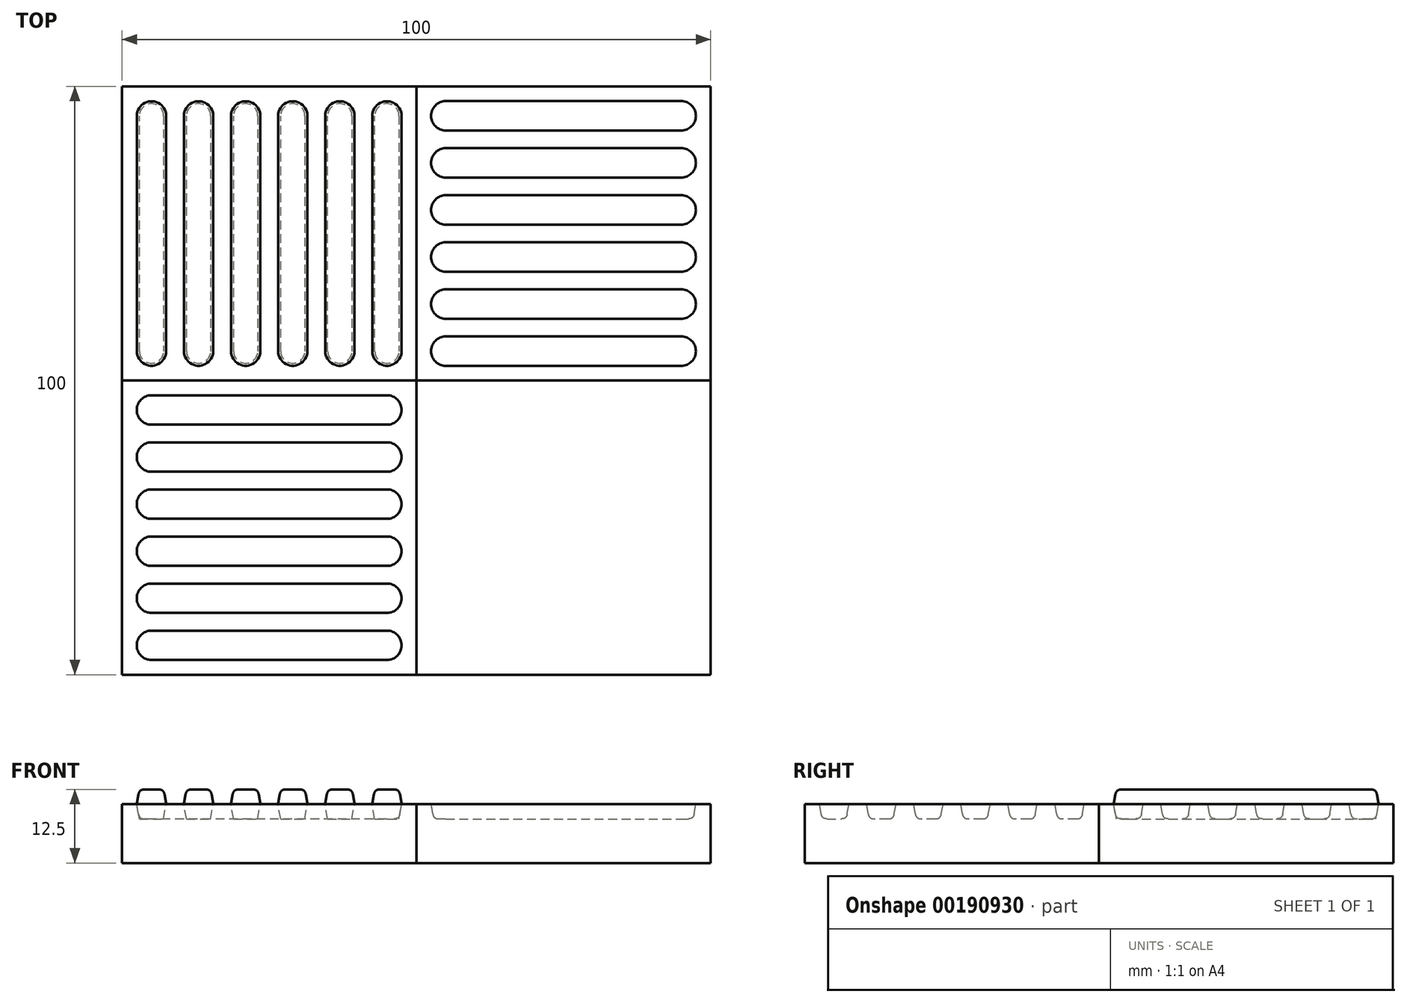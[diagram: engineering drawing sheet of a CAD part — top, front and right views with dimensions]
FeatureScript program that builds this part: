
annotation { "Feature Type Name" : "Feature", "Feature Type Description" : "" }
export const myFeature = defineFeature(function(context is Context, id is Id, definition is map)
    precondition{}
    {
        {
            var Q0;
            Q0=qCreatedBy(makeId("Top.planeOp"),FACE);
            var sketch = newSketch(context, id + "F0", { "sketchPlane" : qUnion([Q0])});
            skLineSegment(sketch, "E0.bottom", {"start": v(0, 0) * mm, "end": v(-50, 0) * mm});
            skLineSegment(sketch, "E0.top", {"start": v(0, 50) * mm, "end": v(-50, 50) * mm});
            skLineSegment(sketch, "E0.left", {"start": v(0, 0) * mm, "end": v(0, 50) * mm});
            skLineSegment(sketch, "E0.right", {"start": v(-50, 0) * mm, "end": v(-50, 50) * mm});
            skPoint(sketch, "E0.middle", {"position": v(-25, 25) * mm});
            skSolve(sketch);
        }
        {
            var Q0;
            Q0=makeQuery(id+"F0.imprint","IMPRINT",FACE,{"disambiguationData":[TD([[makeQuery(id+"F0.imprint","IMPRINT",EDGE,{"derivedFrom":sQuery(id+"F0.wireOp",EDGE,"E0.bottom")}),-1.0]])]});
            extrude(context, id + "F1", {"entities" : qUnion([Q0]), "oppositeDirection" : true, "depth" : 10 * mm});
        }
        {
            var Q0;
            Q0=makeQuery(id+"F1.opExtrude","CAP_FACE",FACE,{"disambiguationData":[OSD([sQuery(id+"F0.wireOp",EDGE,"E0.bottom"),sQuery(id+"F0.wireOp",EDGE,"E0.top"),sQuery(id+"F0.wireOp",EDGE,"E0.left"),sQuery(id+"F0.wireOp",EDGE,"E0.right")])],"isStart":true});
            var sketch = newSketch(context, id + "F2", { "sketchPlane" : qUnion([Q0])});
            skLineSegment(sketch, "E1.bottom", {"start": v(-2.5, 47.5) * mm, "end": v(-47.5, 47.5) * mm, "construction": true});
            skLineSegment(sketch, "E1.top", {"start": v(-2.5, 2.5) * mm, "end": v(-47.5, 2.5) * mm, "construction": true});
            skLineSegment(sketch, "E1.left", {"start": v(-2.5, 47.5) * mm, "end": v(-2.5, 2.5) * mm, "construction": true});
            skLineSegment(sketch, "E1.right", {"start": v(-47.5, 47.5) * mm, "end": v(-47.5, 2.5) * mm, "construction": true});
            skPoint(sketch, "E1.middle", {"position": v(-25, 25) * mm});
            skLineSegment(sketch, "E2", {"start": v(-45, 5) * mm, "end": v(-45, 45) * mm});
            skArc(sketch, "E3.0.startCap", {"start": v(-42.5, 5) * mm, "mid": v(-45, 2.5) * mm, "end": v(-47.5, 5) * mm});
            skArc(sketch, "E3.0.endCap", {"start": v(-47.5, 45) * mm, "mid": v(-45, 47.5) * mm, "end": v(-42.5, 45) * mm});
            skLineSegment(sketch, "E3.0.left", {"start": v(-47.5, 5) * mm, "end": v(-47.5, 45) * mm});
            skLineSegment(sketch, "E3.0.right", {"start": v(-42.5, 5) * mm, "end": v(-42.5, 45) * mm});
            skLineSegment(sketch, "E4.1.0.0", {"start": v(-39.5, 5) * mm, "end": v(-39.5, 45) * mm});
            skArc(sketch, "E4.1.0.1", {"start": v(-39.5, 45) * mm, "mid": v(-37, 47.5) * mm, "end": v(-34.5, 45) * mm});
            skLineSegment(sketch, "E4.1.0.2", {"start": v(-34.5, 5) * mm, "end": v(-34.5, 45) * mm});
            skArc(sketch, "E4.1.0.3", {"start": v(-34.5, 5) * mm, "mid": v(-37, 2.5) * mm, "end": v(-39.5, 5) * mm});
            skLineSegment(sketch, "E4.2.0.0", {"start": v(-31.5, 5) * mm, "end": v(-31.5, 45) * mm});
            skArc(sketch, "E4.2.0.1", {"start": v(-31.5, 45) * mm, "mid": v(-29, 47.5) * mm, "end": v(-26.5, 45) * mm});
            skLineSegment(sketch, "E4.2.0.2", {"start": v(-26.5, 5) * mm, "end": v(-26.5, 45) * mm});
            skArc(sketch, "E4.2.0.3", {"start": v(-26.5, 5) * mm, "mid": v(-29, 2.5) * mm, "end": v(-31.5, 5) * mm});
            skLineSegment(sketch, "E4.3.0.0", {"start": v(-23.5, 5) * mm, "end": v(-23.5, 45) * mm});
            skArc(sketch, "E4.3.0.1", {"start": v(-23.5, 45) * mm, "mid": v(-21, 47.5) * mm, "end": v(-18.5, 45) * mm});
            skLineSegment(sketch, "E4.3.0.2", {"start": v(-18.5, 5) * mm, "end": v(-18.5, 45) * mm});
            skArc(sketch, "E4.3.0.3", {"start": v(-18.5, 5) * mm, "mid": v(-21, 2.5) * mm, "end": v(-23.5, 5) * mm});
            skLineSegment(sketch, "E4.4.0.0", {"start": v(-15.5, 5) * mm, "end": v(-15.5, 45) * mm});
            skArc(sketch, "E4.4.0.1", {"start": v(-15.5, 45) * mm, "mid": v(-13, 47.5) * mm, "end": v(-10.5, 45) * mm});
            skLineSegment(sketch, "E4.4.0.2", {"start": v(-10.5, 5) * mm, "end": v(-10.5, 45) * mm});
            skArc(sketch, "E4.4.0.3", {"start": v(-10.5, 5) * mm, "mid": v(-13, 2.5) * mm, "end": v(-15.5, 5) * mm});
            skLineSegment(sketch, "E4.5.0.0", {"start": v(-7.5, 5) * mm, "end": v(-7.5, 45) * mm});
            skArc(sketch, "E4.5.0.1", {"start": v(-7.5, 45) * mm, "mid": v(-5, 47.5) * mm, "end": v(-2.5, 45) * mm});
            skLineSegment(sketch, "E4.5.0.2", {"start": v(-2.5, 5) * mm, "end": v(-2.5, 45) * mm});
            skArc(sketch, "E4.5.0.3", {"start": v(-2.5, 5) * mm, "mid": v(-5, 2.5) * mm, "end": v(-7.5, 5) * mm});
            skLineSegment(sketch, "E4.direction1", {"start": v(-47.5, 5) * mm, "end": v(-39.5, 5) * mm, "construction": true});
            skSolve(sketch);
        }
        {
            var Q0;
            Q0 = qSketchRegion(id + "F2", true);
            extrude(context, id + "F3", {"entities" : qUnion([Q0]), "depth" : 5 * mm, "hasDraft" : true, "draftAngle" : 10 * degree, "draftPullDirection" : true, "symmetric" : true});
        }
        {
            var Q0;
            Q0=makeQuery(id+"F1.opExtrude","SWEPT_BODY",BODY,{"disambiguationData":[OSD([sQuery(id+"F0.wireOp",EDGE,"E0.bottom"),sQuery(id+"F0.wireOp",EDGE,"E0.top"),sQuery(id+"F0.wireOp",EDGE,"E0.left"),sQuery(id+"F0.wireOp",EDGE,"E0.right")])]});
            var Q1;
            Q1=makeQuery(id+"F3.*.split.splitOp","SPLIT",BODY,{"derivedFrom":makeQuery(id+"F3.opExtrude","SWEPT_BODY",BODY,{"disambiguationData":[OSD([sQuery(id+"F2.wireOp",EDGE,"E3.0.startCap"),sQuery(id+"F2.wireOp",EDGE,"E3.0.endCap"),sQuery(id+"F2.wireOp",EDGE,"E3.0.left"),sQuery(id+"F2.wireOp",EDGE,"E3.0.right")])]})});
            var Q2;
            Q2=makeQuery(id+"F3.*.split.splitOp","SPLIT",BODY,{"derivedFrom":makeQuery(id+"F3.opExtrude","SWEPT_BODY",BODY,{"disambiguationData":[OSD([sQuery(id+"F2.wireOp",EDGE,"E4.1.0.0"),sQuery(id+"F2.wireOp",EDGE,"E4.1.0.1"),sQuery(id+"F2.wireOp",EDGE,"E4.1.0.2"),sQuery(id+"F2.wireOp",EDGE,"E4.1.0.3")])]})});
            var Q3;
            Q3=makeQuery(id+"F3.*.split.splitOp","SPLIT",BODY,{"derivedFrom":makeQuery(id+"F3.opExtrude","SWEPT_BODY",BODY,{"disambiguationData":[OSD([sQuery(id+"F2.wireOp",EDGE,"E4.2.0.0"),sQuery(id+"F2.wireOp",EDGE,"E4.2.0.1"),sQuery(id+"F2.wireOp",EDGE,"E4.2.0.2"),sQuery(id+"F2.wireOp",EDGE,"E4.2.0.3")])]})});
            var Q4;
            Q4=makeQuery(id+"F3.*.split.splitOp","SPLIT",BODY,{"derivedFrom":makeQuery(id+"F3.opExtrude","SWEPT_BODY",BODY,{"disambiguationData":[OSD([sQuery(id+"F2.wireOp",EDGE,"E4.3.0.0"),sQuery(id+"F2.wireOp",EDGE,"E4.3.0.1"),sQuery(id+"F2.wireOp",EDGE,"E4.3.0.2"),sQuery(id+"F2.wireOp",EDGE,"E4.3.0.3")])]})});
            var Q5;
            Q5=makeQuery(id+"F3.*.split.splitOp","SPLIT",BODY,{"derivedFrom":makeQuery(id+"F3.opExtrude","SWEPT_BODY",BODY,{"disambiguationData":[OSD([sQuery(id+"F2.wireOp",EDGE,"E4.4.0.0"),sQuery(id+"F2.wireOp",EDGE,"E4.4.0.1"),sQuery(id+"F2.wireOp",EDGE,"E4.4.0.2"),sQuery(id+"F2.wireOp",EDGE,"E4.4.0.3")])]})});
            var Q6;
            Q6=makeQuery(id+"F3.*.split.splitOp","SPLIT",BODY,{"derivedFrom":makeQuery(id+"F3.opExtrude","SWEPT_BODY",BODY,{"disambiguationData":[OSD([sQuery(id+"F2.wireOp",EDGE,"E4.5.0.0"),sQuery(id+"F2.wireOp",EDGE,"E4.5.0.1"),sQuery(id+"F2.wireOp",EDGE,"E4.5.0.2"),sQuery(id+"F2.wireOp",EDGE,"E4.5.0.3")])]})});
            var Q7;
            Q7=qCreatedBy(makeId("Right.planeOp"),FACE);
            mirror(context, id + "F4", {"entities" : qUnion([Q0, Q1, Q2, Q3, Q4, Q5, Q6]), "mirrorPlane" : qUnion([Q7])});
        }
        {
            var Q0;
            Q0=makeQuery(id+"F4.opPattern","COPY",BODY,{"derivedFrom":makeQuery(id+"F3.*.split.splitOp","SPLIT",BODY,{"derivedFrom":makeQuery(id+"F3.opExtrude","SWEPT_BODY",BODY,{"disambiguationData":[OSD([sQuery(id+"F2.wireOp",EDGE,"E4.5.0.0"),sQuery(id+"F2.wireOp",EDGE,"E4.5.0.1"),sQuery(id+"F2.wireOp",EDGE,"E4.5.0.2"),sQuery(id+"F2.wireOp",EDGE,"E4.5.0.3")])]})}),"instanceName":"1"});
            var Q1;
            Q1=makeQuery(id+"F4.opPattern","COPY",BODY,{"derivedFrom":makeQuery(id+"F3.*.split.splitOp","SPLIT",BODY,{"derivedFrom":makeQuery(id+"F3.opExtrude","SWEPT_BODY",BODY,{"disambiguationData":[OSD([sQuery(id+"F2.wireOp",EDGE,"E4.4.0.0"),sQuery(id+"F2.wireOp",EDGE,"E4.4.0.1"),sQuery(id+"F2.wireOp",EDGE,"E4.4.0.2"),sQuery(id+"F2.wireOp",EDGE,"E4.4.0.3")])]})}),"instanceName":"1"});
            var Q2;
            Q2=makeQuery(id+"F4.opPattern","COPY",BODY,{"derivedFrom":makeQuery(id+"F3.*.split.splitOp","SPLIT",BODY,{"derivedFrom":makeQuery(id+"F3.opExtrude","SWEPT_BODY",BODY,{"disambiguationData":[OSD([sQuery(id+"F2.wireOp",EDGE,"E4.3.0.0"),sQuery(id+"F2.wireOp",EDGE,"E4.3.0.1"),sQuery(id+"F2.wireOp",EDGE,"E4.3.0.2"),sQuery(id+"F2.wireOp",EDGE,"E4.3.0.3")])]})}),"instanceName":"1"});
            var Q3;
            Q3=makeQuery(id+"F4.opPattern","COPY",BODY,{"derivedFrom":makeQuery(id+"F3.*.split.splitOp","SPLIT",BODY,{"derivedFrom":makeQuery(id+"F3.opExtrude","SWEPT_BODY",BODY,{"disambiguationData":[OSD([sQuery(id+"F2.wireOp",EDGE,"E4.2.0.0"),sQuery(id+"F2.wireOp",EDGE,"E4.2.0.1"),sQuery(id+"F2.wireOp",EDGE,"E4.2.0.2"),sQuery(id+"F2.wireOp",EDGE,"E4.2.0.3")])]})}),"instanceName":"1"});
            var Q4;
            Q4=makeQuery(id+"F4.opPattern","COPY",BODY,{"derivedFrom":makeQuery(id+"F3.*.split.splitOp","SPLIT",BODY,{"derivedFrom":makeQuery(id+"F3.opExtrude","SWEPT_BODY",BODY,{"disambiguationData":[OSD([sQuery(id+"F2.wireOp",EDGE,"E4.1.0.0"),sQuery(id+"F2.wireOp",EDGE,"E4.1.0.1"),sQuery(id+"F2.wireOp",EDGE,"E4.1.0.2"),sQuery(id+"F2.wireOp",EDGE,"E4.1.0.3")])]})}),"instanceName":"1"});
            var Q5;
            Q5=makeQuery(id+"F4.opPattern","COPY",BODY,{"derivedFrom":makeQuery(id+"F3.*.split.splitOp","SPLIT",BODY,{"derivedFrom":makeQuery(id+"F3.opExtrude","SWEPT_BODY",BODY,{"disambiguationData":[OSD([sQuery(id+"F2.wireOp",EDGE,"E3.0.startCap"),sQuery(id+"F2.wireOp",EDGE,"E3.0.endCap"),sQuery(id+"F2.wireOp",EDGE,"E3.0.left"),sQuery(id+"F2.wireOp",EDGE,"E3.0.right")])]})}),"instanceName":"1"});
            var Q6;
            Q6=makeQuery(id+"F4.opPattern","COPY",BODY,{"derivedFrom":makeQuery(id+"F1.opExtrude","SWEPT_BODY",BODY,{"disambiguationData":[OSD([sQuery(id+"F0.wireOp",EDGE,"E0.bottom"),sQuery(id+"F0.wireOp",EDGE,"E0.top"),sQuery(id+"F0.wireOp",EDGE,"E0.left"),sQuery(id+"F0.wireOp",EDGE,"E0.right")])]}),"instanceName":"1"});
            booleanBodies(context, id + "F5", {"operationType" : BooleanOperationType.SUBTRACTION, "tools" : qUnion([Q0, Q1, Q2, Q3, Q4, Q5]), "targets" : qUnion([Q6])});
        }
        {
            var Q0;
            Q0=makeQuery(id+"F3.opExtrude","CAP_FACE",FACE,{"disambiguationData":[OSD([sQuery(id+"F2.wireOp",EDGE,"E3.0.startCap"),sQuery(id+"F2.wireOp",EDGE,"E3.0.endCap"),sQuery(id+"F2.wireOp",EDGE,"E3.0.left"),sQuery(id+"F2.wireOp",EDGE,"E3.0.right")])],"isStart":false});
            var Q1;
            Q1=makeQuery(id+"F3.opExtrude","CAP_FACE",FACE,{"disambiguationData":[OSD([sQuery(id+"F2.wireOp",EDGE,"E4.1.0.0"),sQuery(id+"F2.wireOp",EDGE,"E4.1.0.1"),sQuery(id+"F2.wireOp",EDGE,"E4.1.0.2"),sQuery(id+"F2.wireOp",EDGE,"E4.1.0.3")])],"isStart":false});
            var Q2;
            Q2=makeQuery(id+"F3.opExtrude","CAP_FACE",FACE,{"disambiguationData":[OSD([sQuery(id+"F2.wireOp",EDGE,"E4.2.0.0"),sQuery(id+"F2.wireOp",EDGE,"E4.2.0.1"),sQuery(id+"F2.wireOp",EDGE,"E4.2.0.2"),sQuery(id+"F2.wireOp",EDGE,"E4.2.0.3")])],"isStart":false});
            var Q3;
            Q3=makeQuery(id+"F3.opExtrude","CAP_FACE",FACE,{"disambiguationData":[OSD([sQuery(id+"F2.wireOp",EDGE,"E4.3.0.0"),sQuery(id+"F2.wireOp",EDGE,"E4.3.0.1"),sQuery(id+"F2.wireOp",EDGE,"E4.3.0.2"),sQuery(id+"F2.wireOp",EDGE,"E4.3.0.3")])],"isStart":false});
            var Q4;
            Q4=makeQuery(id+"F3.opExtrude","CAP_FACE",FACE,{"disambiguationData":[OSD([sQuery(id+"F2.wireOp",EDGE,"E4.4.0.0"),sQuery(id+"F2.wireOp",EDGE,"E4.4.0.1"),sQuery(id+"F2.wireOp",EDGE,"E4.4.0.2"),sQuery(id+"F2.wireOp",EDGE,"E4.4.0.3")])],"isStart":false});
            var Q5;
            Q5=makeQuery(id+"F3.opExtrude","CAP_FACE",FACE,{"disambiguationData":[OSD([sQuery(id+"F2.wireOp",EDGE,"E4.5.0.0"),sQuery(id+"F2.wireOp",EDGE,"E4.5.0.1"),sQuery(id+"F2.wireOp",EDGE,"E4.5.0.2"),sQuery(id+"F2.wireOp",EDGE,"E4.5.0.3")])],"isStart":false});
            var Q6;
            Q6=makeQuery(id+"F5.opBoolean","COPY",FACE,{"derivedFrom":makeQuery(id+"F4.opPattern","COPY",FACE,{"derivedFrom":makeQuery(id+"F3.opExtrude","CAP_FACE",FACE,{"disambiguationData":[OSD([sQuery(id+"F2.wireOp",EDGE,"E4.5.0.0"),sQuery(id+"F2.wireOp",EDGE,"E4.5.0.1"),sQuery(id+"F2.wireOp",EDGE,"E4.5.0.2"),sQuery(id+"F2.wireOp",EDGE,"E4.5.0.3")])],"isStart":true}),"instanceName":"1"})});
            var Q7;
            Q7=makeQuery(id+"F5.opBoolean","COPY",FACE,{"derivedFrom":makeQuery(id+"F4.opPattern","COPY",FACE,{"derivedFrom":makeQuery(id+"F3.opExtrude","CAP_FACE",FACE,{"disambiguationData":[OSD([sQuery(id+"F2.wireOp",EDGE,"E4.4.0.0"),sQuery(id+"F2.wireOp",EDGE,"E4.4.0.1"),sQuery(id+"F2.wireOp",EDGE,"E4.4.0.2"),sQuery(id+"F2.wireOp",EDGE,"E4.4.0.3")])],"isStart":true}),"instanceName":"1"})});
            var Q8;
            Q8=makeQuery(id+"F5.opBoolean","COPY",FACE,{"derivedFrom":makeQuery(id+"F4.opPattern","COPY",FACE,{"derivedFrom":makeQuery(id+"F3.opExtrude","CAP_FACE",FACE,{"disambiguationData":[OSD([sQuery(id+"F2.wireOp",EDGE,"E4.3.0.0"),sQuery(id+"F2.wireOp",EDGE,"E4.3.0.1"),sQuery(id+"F2.wireOp",EDGE,"E4.3.0.2"),sQuery(id+"F2.wireOp",EDGE,"E4.3.0.3")])],"isStart":true}),"instanceName":"1"})});
            var Q9;
            Q9=makeQuery(id+"F5.opBoolean","COPY",FACE,{"derivedFrom":makeQuery(id+"F4.opPattern","COPY",FACE,{"derivedFrom":makeQuery(id+"F3.opExtrude","CAP_FACE",FACE,{"disambiguationData":[OSD([sQuery(id+"F2.wireOp",EDGE,"E4.2.0.0"),sQuery(id+"F2.wireOp",EDGE,"E4.2.0.1"),sQuery(id+"F2.wireOp",EDGE,"E4.2.0.2"),sQuery(id+"F2.wireOp",EDGE,"E4.2.0.3")])],"isStart":true}),"instanceName":"1"})});
            var Q10;
            Q10=makeQuery(id+"F5.opBoolean","COPY",FACE,{"derivedFrom":makeQuery(id+"F4.opPattern","COPY",FACE,{"derivedFrom":makeQuery(id+"F3.opExtrude","CAP_FACE",FACE,{"disambiguationData":[OSD([sQuery(id+"F2.wireOp",EDGE,"E4.1.0.0"),sQuery(id+"F2.wireOp",EDGE,"E4.1.0.1"),sQuery(id+"F2.wireOp",EDGE,"E4.1.0.2"),sQuery(id+"F2.wireOp",EDGE,"E4.1.0.3")])],"isStart":true}),"instanceName":"1"})});
            var Q11;
            Q11=makeQuery(id+"F5.opBoolean","COPY",FACE,{"derivedFrom":makeQuery(id+"F4.opPattern","COPY",FACE,{"derivedFrom":makeQuery(id+"F3.opExtrude","CAP_FACE",FACE,{"disambiguationData":[OSD([sQuery(id+"F2.wireOp",EDGE,"E3.0.startCap"),sQuery(id+"F2.wireOp",EDGE,"E3.0.endCap"),sQuery(id+"F2.wireOp",EDGE,"E3.0.left"),sQuery(id+"F2.wireOp",EDGE,"E3.0.right")])],"isStart":true}),"instanceName":"1"})});
            fillet(context, id + "F6", {"entities" : qUnion([Q0, Q1, Q2, Q3, Q4, Q5, Q6, Q7, Q8, Q9, Q10, Q11]), "radius" : 1 * mm, "tangentPropagation" : true, "rho" : 0.5, "crossSection" : FilletCrossSection.CONIC, "allowEdgeOverflow" : false});
        }
        {
            var Q0;
            {var subQ0=makeQuery(id+"F3.opExtrude","SWEPT_FACE",FACE,{"disambiguationData":[OSD([sQuery(id+"F2.wireOp",EDGE,"E3.0.left")])]});Q0=makeQuery(id+"F3.*.booleanUnion.opBoolean","MERGE",EDGE,{"derivedFrom":[makeQuery(id+"F3.*.split.splitOp","SPLIT_SURFACE_INTERSECT",EDGE,{"derivedFrom":[subQ0]}),makeQuery(id+"F3.*.split.splitOp","SPLIT_SURFACE_INTERSECT",EDGE,{"derivedFrom":[subQ0],"isFromBackBody":true})]});}
            var Q1;
            {var subQ0=makeQuery(id+"F3.opExtrude","SWEPT_FACE",FACE,{"disambiguationData":[OSD([sQuery(id+"F2.wireOp",EDGE,"E4.1.0.0")])]});Q1=makeQuery(id+"F3.*.booleanUnion.opBoolean","MERGE",EDGE,{"derivedFrom":[makeQuery(id+"F3.*.split.splitOp","SPLIT_SURFACE_INTERSECT",EDGE,{"derivedFrom":[subQ0]}),makeQuery(id+"F3.*.split.splitOp","SPLIT_SURFACE_INTERSECT",EDGE,{"derivedFrom":[subQ0],"isFromBackBody":true})]});}
            var Q2;
            {var subQ0=makeQuery(id+"F3.opExtrude","SWEPT_FACE",FACE,{"disambiguationData":[OSD([sQuery(id+"F2.wireOp",EDGE,"E4.2.0.0")])]});Q2=makeQuery(id+"F3.*.booleanUnion.opBoolean","MERGE",EDGE,{"derivedFrom":[makeQuery(id+"F3.*.split.splitOp","SPLIT_SURFACE_INTERSECT",EDGE,{"derivedFrom":[subQ0]}),makeQuery(id+"F3.*.split.splitOp","SPLIT_SURFACE_INTERSECT",EDGE,{"derivedFrom":[subQ0],"isFromBackBody":true})]});}
            var Q3;
            {var subQ0=makeQuery(id+"F3.opExtrude","SWEPT_FACE",FACE,{"disambiguationData":[OSD([sQuery(id+"F2.wireOp",EDGE,"E4.3.0.0")])]});Q3=makeQuery(id+"F3.*.booleanUnion.opBoolean","MERGE",EDGE,{"derivedFrom":[makeQuery(id+"F3.*.split.splitOp","SPLIT_SURFACE_INTERSECT",EDGE,{"derivedFrom":[subQ0]}),makeQuery(id+"F3.*.split.splitOp","SPLIT_SURFACE_INTERSECT",EDGE,{"derivedFrom":[subQ0],"isFromBackBody":true})]});}
            var Q4;
            {var subQ0=makeQuery(id+"F3.opExtrude","SWEPT_FACE",FACE,{"disambiguationData":[OSD([sQuery(id+"F2.wireOp",EDGE,"E4.4.0.0")])]});Q4=makeQuery(id+"F3.*.booleanUnion.opBoolean","MERGE",EDGE,{"derivedFrom":[makeQuery(id+"F3.*.split.splitOp","SPLIT_SURFACE_INTERSECT",EDGE,{"derivedFrom":[subQ0]}),makeQuery(id+"F3.*.split.splitOp","SPLIT_SURFACE_INTERSECT",EDGE,{"derivedFrom":[subQ0],"isFromBackBody":true})]});}
            var Q5;
            {var subQ0=makeQuery(id+"F3.opExtrude","SWEPT_FACE",FACE,{"disambiguationData":[OSD([sQuery(id+"F2.wireOp",EDGE,"E4.5.0.0")])]});Q5=makeQuery(id+"F3.*.booleanUnion.opBoolean","MERGE",EDGE,{"derivedFrom":[makeQuery(id+"F3.*.split.splitOp","SPLIT_SURFACE_INTERSECT",EDGE,{"derivedFrom":[subQ0]}),makeQuery(id+"F3.*.split.splitOp","SPLIT_SURFACE_INTERSECT",EDGE,{"derivedFrom":[subQ0],"isFromBackBody":true})]});}
            var Q6;
            {var subQ0=makeQuery(id+"F3.opExtrude","SWEPT_FACE",FACE,{"disambiguationData":[OSD([sQuery(id+"F2.wireOp",EDGE,"E4.5.0.2")])]});Q6=makeQuery(id+"F5.opBoolean","COPY",EDGE,{"derivedFrom":makeQuery(id+"F4.opPattern","COPY",EDGE,{"derivedFrom":makeQuery(id+"F3.*.booleanUnion.opBoolean","MERGE",EDGE,{"derivedFrom":[makeQuery(id+"F3.*.split.splitOp","SPLIT_SURFACE_INTERSECT",EDGE,{"derivedFrom":[subQ0]}),makeQuery(id+"F3.*.split.splitOp","SPLIT_SURFACE_INTERSECT",EDGE,{"derivedFrom":[subQ0],"isFromBackBody":true})]}),"instanceName":"1"})});}
            var Q7;
            {var subQ0=makeQuery(id+"F3.opExtrude","SWEPT_FACE",FACE,{"disambiguationData":[OSD([sQuery(id+"F2.wireOp",EDGE,"E4.4.0.2")])]});Q7=makeQuery(id+"F5.opBoolean","COPY",EDGE,{"derivedFrom":makeQuery(id+"F4.opPattern","COPY",EDGE,{"derivedFrom":makeQuery(id+"F3.*.booleanUnion.opBoolean","MERGE",EDGE,{"derivedFrom":[makeQuery(id+"F3.*.split.splitOp","SPLIT_SURFACE_INTERSECT",EDGE,{"derivedFrom":[subQ0]}),makeQuery(id+"F3.*.split.splitOp","SPLIT_SURFACE_INTERSECT",EDGE,{"derivedFrom":[subQ0],"isFromBackBody":true})]}),"instanceName":"1"})});}
            var Q8;
            {var subQ0=makeQuery(id+"F3.opExtrude","SWEPT_FACE",FACE,{"disambiguationData":[OSD([sQuery(id+"F2.wireOp",EDGE,"E4.3.0.2")])]});Q8=makeQuery(id+"F5.opBoolean","COPY",EDGE,{"derivedFrom":makeQuery(id+"F4.opPattern","COPY",EDGE,{"derivedFrom":makeQuery(id+"F3.*.booleanUnion.opBoolean","MERGE",EDGE,{"derivedFrom":[makeQuery(id+"F3.*.split.splitOp","SPLIT_SURFACE_INTERSECT",EDGE,{"derivedFrom":[subQ0]}),makeQuery(id+"F3.*.split.splitOp","SPLIT_SURFACE_INTERSECT",EDGE,{"derivedFrom":[subQ0],"isFromBackBody":true})]}),"instanceName":"1"})});}
            var Q9;
            {var subQ0=makeQuery(id+"F3.opExtrude","SWEPT_FACE",FACE,{"disambiguationData":[OSD([sQuery(id+"F2.wireOp",EDGE,"E4.2.0.2")])]});Q9=makeQuery(id+"F5.opBoolean","COPY",EDGE,{"derivedFrom":makeQuery(id+"F4.opPattern","COPY",EDGE,{"derivedFrom":makeQuery(id+"F3.*.booleanUnion.opBoolean","MERGE",EDGE,{"derivedFrom":[makeQuery(id+"F3.*.split.splitOp","SPLIT_SURFACE_INTERSECT",EDGE,{"derivedFrom":[subQ0]}),makeQuery(id+"F3.*.split.splitOp","SPLIT_SURFACE_INTERSECT",EDGE,{"derivedFrom":[subQ0],"isFromBackBody":true})]}),"instanceName":"1"})});}
            var Q10;
            {var subQ0=makeQuery(id+"F3.opExtrude","SWEPT_FACE",FACE,{"disambiguationData":[OSD([sQuery(id+"F2.wireOp",EDGE,"E4.1.0.2")])]});Q10=makeQuery(id+"F5.opBoolean","COPY",EDGE,{"derivedFrom":makeQuery(id+"F4.opPattern","COPY",EDGE,{"derivedFrom":makeQuery(id+"F3.*.booleanUnion.opBoolean","MERGE",EDGE,{"derivedFrom":[makeQuery(id+"F3.*.split.splitOp","SPLIT_SURFACE_INTERSECT",EDGE,{"derivedFrom":[subQ0]}),makeQuery(id+"F3.*.split.splitOp","SPLIT_SURFACE_INTERSECT",EDGE,{"derivedFrom":[subQ0],"isFromBackBody":true})]}),"instanceName":"1"})});}
            var Q11;
            {var subQ0=makeQuery(id+"F3.opExtrude","SWEPT_FACE",FACE,{"disambiguationData":[OSD([sQuery(id+"F2.wireOp",EDGE,"E3.0.right")])]});Q11=makeQuery(id+"F5.opBoolean","COPY",EDGE,{"derivedFrom":makeQuery(id+"F4.opPattern","COPY",EDGE,{"derivedFrom":makeQuery(id+"F3.*.booleanUnion.opBoolean","MERGE",EDGE,{"derivedFrom":[makeQuery(id+"F3.*.split.splitOp","SPLIT_SURFACE_INTERSECT",EDGE,{"derivedFrom":[subQ0]}),makeQuery(id+"F3.*.split.splitOp","SPLIT_SURFACE_INTERSECT",EDGE,{"derivedFrom":[subQ0],"isFromBackBody":true})]}),"instanceName":"1"})});}
            fillet(context, id + "F7", {"entities" : qUnion([Q0, Q1, Q2, Q3, Q4, Q5, Q6, Q7, Q8, Q9, Q10, Q11]), "radius" : 1 * mm, "tangentPropagation" : true, "rho" : 0.5, "crossSection" : FilletCrossSection.CONIC, "allowEdgeOverflow" : false});
        }
        {
            var Q0;
            Q0=qCreatedBy(makeId("Right.planeOp"),FACE);
            var Q1;
            Q1=makeQuery(id+"F4.opPattern","COPY",FACE,{"derivedFrom":makeQuery(id+"F1.opExtrude","SWEPT_FACE",FACE,{"disambiguationData":[OSD([sQuery(id+"F0.wireOp",EDGE,"E0.right")])]}),"instanceName":"1"});
            cPlane(context, id + "F8", {"entities" : qUnion([Q0, Q1]), "cplaneType" : CPlaneType.MID_PLANE, "offset" : 25 * mm, "width" : 150 * mm, "height" : 150 * mm});
        }
        {
            var Q0;
            Q0=qCreatedBy(id+"F8.planeOp",FACE);
            var sketch = newSketch(context, id + "F9", { "sketchPlane" : qUnion([Q0])});
            skLineSegment(sketch, "E5", {"start": v(50, -10) * mm, "end": v(0, -10) * mm, "construction": true});
            skLineSegment(sketch, "E6", {"start": v(25, -10) * mm, "end": v(25, 17.17) * mm, "construction": true});
            skSolve(sketch);
        }
        {
            var Q0;
            Q0=makeQuery(id+"F4.opPattern","COPY",BODY,{"derivedFrom":makeQuery(id+"F1.opExtrude","SWEPT_BODY",BODY,{"disambiguationData":[OSD([sQuery(id+"F0.wireOp",EDGE,"E0.bottom"),sQuery(id+"F0.wireOp",EDGE,"E0.top"),sQuery(id+"F0.wireOp",EDGE,"E0.left"),sQuery(id+"F0.wireOp",EDGE,"E0.right")])]}),"instanceName":"1"});
            var Q1;
            Q1=sQuery(id+"F9.wireOp",EDGE,"E6");
            transform(context, id + "F10", {"entities" : qUnion([Q0]), "transformType" : TransformType.ROTATION, "transformAxis" : qUnion([Q1]), "angle" : 90 * degree, "makeCopy" : false});
        }
        {
            var Q0;
            Q0=makeQuery(id+"F1.opExtrude","SWEPT_BODY",BODY,{"disambiguationData":[OSD([sQuery(id+"F0.wireOp",EDGE,"E0.bottom"),sQuery(id+"F0.wireOp",EDGE,"E0.top"),sQuery(id+"F0.wireOp",EDGE,"E0.left"),sQuery(id+"F0.wireOp",EDGE,"E0.right")])]});
            var Q1;
            Q1=makeQuery(id+"F4.opPattern","COPY",BODY,{"derivedFrom":makeQuery(id+"F1.opExtrude","SWEPT_BODY",BODY,{"disambiguationData":[OSD([sQuery(id+"F0.wireOp",EDGE,"E0.bottom"),sQuery(id+"F0.wireOp",EDGE,"E0.top"),sQuery(id+"F0.wireOp",EDGE,"E0.left"),sQuery(id+"F0.wireOp",EDGE,"E0.right")])]}),"instanceName":"1"});
            var Q2;
            Q2=makeQuery(id+"F1.opExtrude","SWEPT_EDGE",EDGE,{"disambiguationData":[OSD([sQuery(id+"F0.wireOp",EDGE,"E0.bottom"),sQuery(id+"F0.wireOp",EDGE,"E0.left")])]});
            transform(context, id + "F11", {"entities" : qUnion([Q0, Q1]), "transformType" : TransformType.ROTATION, "transformAxis" : qUnion([Q2]), "angle" : 180 * degree, "makeCopy" : true});
        }
    });
